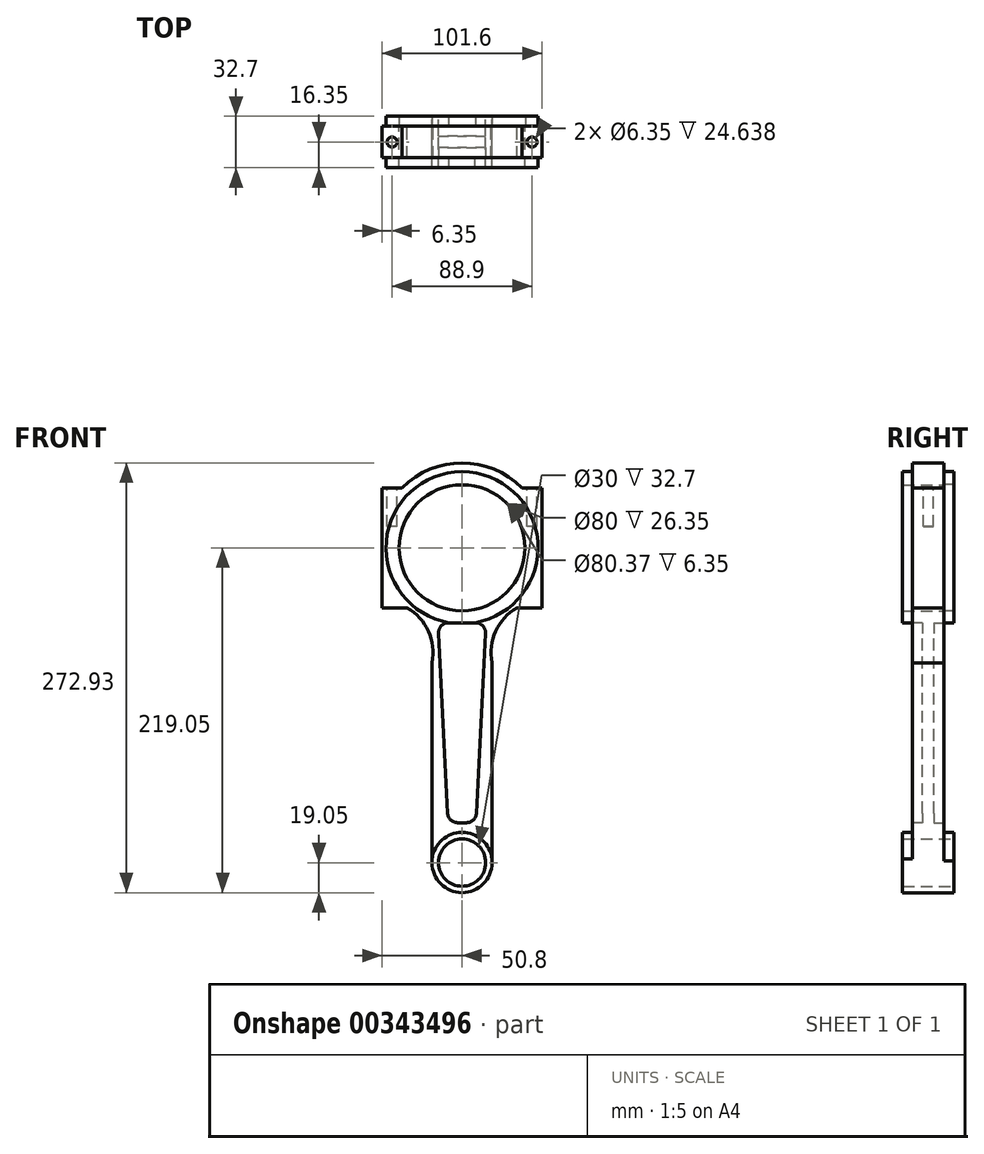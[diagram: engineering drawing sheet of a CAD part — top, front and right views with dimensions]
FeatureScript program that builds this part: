
annotation { "Feature Type Name" : "Feature", "Feature Type Description" : "" }
export const myFeature = defineFeature(function(context is Context, id is Id, definition is map)
    precondition{}
    {
        {
            var Q0;
            Q0=qCreatedBy(makeId("Front.planeOp"),FACE);
            var sketch = newSketch(context, id + "F0", { "sketchPlane" : qUnion([Q0])});
            skCircle(sketch, "E0", {"center": v(0, 0) * mm, "radius": 15 * mm});
            skCircle(sketch, "E1", {"center": v(0, 200) * mm, "radius": 40 * mm});
            skLineSegment(sketch, "E2", {"start": v(-50.8, 238.1) * mm, "end": v(-50.8, 161.9) * mm});
            skLineSegment(sketch, "E3", {"start": v(-50.8, 161.9) * mm, "end": v(-34.85, 161.9) * mm});
            skArc(sketch, "E4", {"start": v(-19.05, 127) * mm, "mid": v(-21.36, 146.98) * mm, "end": v(-34.85, 161.9) * mm});
            skLineSegment(sketch, "E5", {"start": v(-19.05, 127) * mm, "end": v(-19.05, 0) * mm});
            skLineSegment(sketch, "E6.MirrorCS", {"start": v(19.05, 127) * mm, "end": v(19.05, 0) * mm});
            skArc(sketch, "E7.MirrorCS", {"start": v(19.05, 127) * mm, "mid": v(21.36, 146.98) * mm, "end": v(34.85, 161.9) * mm});
            skLineSegment(sketch, "E8.MirrorCS", {"start": v(50.8, 238.1) * mm, "end": v(50.8, 161.9) * mm});
            skLineSegment(sketch, "E9.MirrorCS", {"start": v(50.8, 161.9) * mm, "end": v(34.85, 161.9) * mm});
            skLineSegment(sketch, "E10", {"start": v(-50.8, 238.1) * mm, "end": v(-38.1, 238.1) * mm});
            skLineSegment(sketch, "E11.MirrorCS", {"start": v(50.8, 238.1) * mm, "end": v(38.1, 238.1) * mm});
            skArc(sketch, "E12", {"start": v(38.1, 238.1) * mm, "mid": v(0, 253.88) * mm, "end": v(-38.1, 238.1) * mm});
            skArc(sketch, "E13", {"start": v(-19.05, 0) * mm, "mid": v(0, -19.05) * mm, "end": v(19.05, 0) * mm});
            skSolve(sketch);
        }
        {
            var Q0;
            Q0=makeQuery(id+"F0.imprint","IMPRINT",FACE,{"disambiguationData":[TD([[makeQuery(id+"F0.imprint","IMPRINT",EDGE,{"derivedFrom":sQuery(id+"F0.wireOp",EDGE,"E0")}),-1.0]])]});
            extrude(context, id + "F1", {"entities" : qUnion([Q0]), "endBound" : BoundingType.SYMMETRIC, "depth" : 20 * mm});
        }
        {
            var Q0;
            Q0=makeQuery(id+"F1.opExtrude","CAP_FACE",FACE,{"disambiguationData":[OSD([sQuery(id+"F0.wireOp",EDGE,"E0"),sQuery(id+"F0.wireOp",EDGE,"E1"),sQuery(id+"F0.wireOp",EDGE,"E2"),sQuery(id+"F0.wireOp",EDGE,"E3"),sQuery(id+"F0.wireOp",EDGE,"E4"),sQuery(id+"F0.wireOp",EDGE,"E5"),sQuery(id+"F0.wireOp",EDGE,"E6.MirrorCS"),sQuery(id+"F0.wireOp",EDGE,"E7.MirrorCS"),sQuery(id+"F0.wireOp",EDGE,"E8.MirrorCS"),sQuery(id+"F0.wireOp",EDGE,"E9.MirrorCS"),sQuery(id+"F0.wireOp",EDGE,"E10"),sQuery(id+"F0.wireOp",EDGE,"E11.MirrorCS"),sQuery(id+"F0.wireOp",EDGE,"E12"),sQuery(id+"F0.wireOp",EDGE,"E13")])],"isStart":true});
            var sketch = newSketch(context, id + "F2", { "sketchPlane" : qUnion([Q0])});
            skLineSegment(sketch, "E14", {"start": v(-8.56, 152.4) * mm, "end": v(8.56, 152.4) * mm});
            skLineSegment(sketch, "E15", {"start": v(14.9, 145.73) * mm, "end": v(9.2, 31.43) * mm});
            skLineSegment(sketch, "E16", {"start": v(2.85, 25.4) * mm, "end": v(-2.85, 25.4) * mm});
            skLineSegment(sketch, "E17", {"start": v(-9.2, 31.43) * mm, "end": v(-14.9, 145.73) * mm});
            skPoint(sketch, "E18.visualSharp", {"position": v(-15.24, 152.4) * mm});
            skArc(sketch, "E18.filletArc", {"start": v(-8.56, 152.4) * mm, "mid": v(-13.17, 150.43) * mm, "end": v(-14.9, 145.73) * mm});
            skPoint(sketch, "E19.visualSharp", {"position": v(15.24, 152.4) * mm});
            skArc(sketch, "E19.filletArc", {"start": v(14.9, 145.73) * mm, "mid": v(13.17, 150.43) * mm, "end": v(8.56, 152.4) * mm});
            skPoint(sketch, "E20.visualSharp", {"position": v(-8.9, 25.4) * mm});
            skArc(sketch, "E20.filletArc", {"start": v(-9.2, 31.43) * mm, "mid": v(-7.23, 27.15) * mm, "end": v(-2.85, 25.4) * mm});
            skPoint(sketch, "E21.visualSharp", {"position": v(8.89, 25.4) * mm});
            skArc(sketch, "E21.filletArc", {"start": v(2.85, 25.4) * mm, "mid": v(7.23, 27.15) * mm, "end": v(9.2, 31.43) * mm});
            skSolve(sketch);
        }
        {
            var Q0;
            Q0=makeQuery(id+"F2.imprint","IMPRINT",FACE,{"disambiguationData":[TD([[makeQuery(id+"F2.imprint","IMPRINT",EDGE,{"derivedFrom":sQuery(id+"F2.wireOp",EDGE,"E14")}),-1.0]])]});
            extrude(context, id + "F3", {"entities" : qUnion([Q0]), "operationType" : NewBodyOperationType.REMOVE, "oppositeDirection" : true, "depth" : 6.35 * mm});
        }
        {
            var Q0;
            Q0=makeQuery(id+"F1.opExtrude","CAP_FACE",FACE,{"disambiguationData":[OSD([sQuery(id+"F0.wireOp",EDGE,"E0"),sQuery(id+"F0.wireOp",EDGE,"E1"),sQuery(id+"F0.wireOp",EDGE,"E2"),sQuery(id+"F0.wireOp",EDGE,"E3"),sQuery(id+"F0.wireOp",EDGE,"E4"),sQuery(id+"F0.wireOp",EDGE,"E5"),sQuery(id+"F0.wireOp",EDGE,"E6.MirrorCS"),sQuery(id+"F0.wireOp",EDGE,"E7.MirrorCS"),sQuery(id+"F0.wireOp",EDGE,"E8.MirrorCS"),sQuery(id+"F0.wireOp",EDGE,"E9.MirrorCS"),sQuery(id+"F0.wireOp",EDGE,"E10"),sQuery(id+"F0.wireOp",EDGE,"E11.MirrorCS"),sQuery(id+"F0.wireOp",EDGE,"E12"),sQuery(id+"F0.wireOp",EDGE,"E13")])],"isStart":false});
            var sketch = newSketch(context, id + "F4", { "sketchPlane" : qUnion([Q0])});
            skLineSegment(sketch, "E22", {"start": v(-8.57, 152.4) * mm, "end": v(8.56, 152.4) * mm});
            skLineSegment(sketch, "E23", {"start": v(14.9, 145.73) * mm, "end": v(9.19, 31.43) * mm});
            skLineSegment(sketch, "E24", {"start": v(2.84, 25.4) * mm, "end": v(-2.85, 25.4) * mm});
            skLineSegment(sketch, "E25", {"start": v(-9.2, 31.43) * mm, "end": v(-14.91, 145.73) * mm});
            skPoint(sketch, "E26.visualSharp", {"position": v(-15.24, 152.4) * mm});
            skArc(sketch, "E26.filletArc", {"start": v(-8.57, 152.4) * mm, "mid": v(-13.17, 150.43) * mm, "end": v(-14.91, 145.73) * mm});
            skPoint(sketch, "E27.visualSharp", {"position": v(15.24, 152.4) * mm});
            skArc(sketch, "E27.filletArc", {"start": v(14.9, 145.73) * mm, "mid": v(13.16, 150.43) * mm, "end": v(8.56, 152.4) * mm});
            skPoint(sketch, "E28.visualSharp", {"position": v(-8.9, 25.4) * mm});
            skArc(sketch, "E28.filletArc", {"start": v(-9.2, 31.43) * mm, "mid": v(-7.23, 27.15) * mm, "end": v(-2.85, 25.4) * mm});
            skPoint(sketch, "E29.visualSharp", {"position": v(8.89, 25.4) * mm});
            skArc(sketch, "E29.filletArc", {"start": v(2.84, 25.4) * mm, "mid": v(7.22, 27.15) * mm, "end": v(9.19, 31.43) * mm});
            skSolve(sketch);
        }
        {
            var Q0;
            Q0=makeQuery(id+"F4.imprint","IMPRINT",FACE,{"disambiguationData":[TD([[makeQuery(id+"F4.imprint","IMPRINT",EDGE,{"derivedFrom":sQuery(id+"F4.wireOp",EDGE,"E22")}),-1.0]])]});
            extrude(context, id + "F5", {"entities" : qUnion([Q0]), "operationType" : NewBodyOperationType.REMOVE, "oppositeDirection" : true, "depth" : 6.35 * mm});
        }
        {
            var Q0;
            Q0=makeQuery(id+"F1.opExtrude","CAP_FACE",FACE,{"disambiguationData":[OSD([sQuery(id+"F0.wireOp",EDGE,"E0"),sQuery(id+"F0.wireOp",EDGE,"E1"),sQuery(id+"F0.wireOp",EDGE,"E2"),sQuery(id+"F0.wireOp",EDGE,"E3"),sQuery(id+"F0.wireOp",EDGE,"E4"),sQuery(id+"F0.wireOp",EDGE,"E5"),sQuery(id+"F0.wireOp",EDGE,"E6.MirrorCS"),sQuery(id+"F0.wireOp",EDGE,"E7.MirrorCS"),sQuery(id+"F0.wireOp",EDGE,"E8.MirrorCS"),sQuery(id+"F0.wireOp",EDGE,"E9.MirrorCS"),sQuery(id+"F0.wireOp",EDGE,"E10"),sQuery(id+"F0.wireOp",EDGE,"E11.MirrorCS"),sQuery(id+"F0.wireOp",EDGE,"E12"),sQuery(id+"F0.wireOp",EDGE,"E13")])],"isStart":false});
            var sketch = newSketch(context, id + "F6", { "sketchPlane" : qUnion([Q0])});
            skCircle(sketch, "E30", {"center": v(0, 0) * mm, "radius": 14.78 * mm});
            skCircle(sketch, "E31", {"center": v(0, 0) * mm, "radius": 19.18 * mm});
            skCircle(sketch, "E32", {"center": v(0, 200) * mm, "radius": 39.98 * mm});
            skCircle(sketch, "E33", {"center": v(0, 200) * mm, "radius": 48.3 * mm});
            skSolve(sketch);
        }
        {
            var Q0;
            Q0=makeQuery(id+"F6.imprint","IMPRINT",FACE,{"disambiguationData":[TD([[makeQuery(id+"F6.imprint","IMPRINT",EDGE,{"derivedFrom":makeQuery(id+"F1.opExtrude","CAP_EDGE",EDGE,{"disambiguationData":[OSD([sQuery(id+"F0.wireOp",EDGE,"E1")])],"isStart":false})}),-1.0]])]});
            var Q1;
            Q1=makeQuery(id+"F6.imprint","IMPRINT",FACE,{"disambiguationData":[TD([[makeQuery(id+"F6.imprint","IMPRINT",EDGE,{"derivedFrom":makeQuery(id+"F1.opExtrude","CAP_EDGE",EDGE,{"disambiguationData":[OSD([sQuery(id+"F0.wireOp",EDGE,"E0")])],"isStart":false})}),-1.0]])]});
            extrude(context, id + "F7", {"entities" : qUnion([Q0, Q1]), "operationType" : NewBodyOperationType.ADD, "endBound" : BoundingType.SYMMETRIC, "depth" : 12.7 * mm});
        }
        {
            var Q0;
            Q0=makeQuery(id+"F1.opExtrude","CAP_FACE",FACE,{"disambiguationData":[OSD([sQuery(id+"F0.wireOp",EDGE,"E0"),sQuery(id+"F0.wireOp",EDGE,"E1"),sQuery(id+"F0.wireOp",EDGE,"E2"),sQuery(id+"F0.wireOp",EDGE,"E3"),sQuery(id+"F0.wireOp",EDGE,"E4"),sQuery(id+"F0.wireOp",EDGE,"E5"),sQuery(id+"F0.wireOp",EDGE,"E6.MirrorCS"),sQuery(id+"F0.wireOp",EDGE,"E7.MirrorCS"),sQuery(id+"F0.wireOp",EDGE,"E8.MirrorCS"),sQuery(id+"F0.wireOp",EDGE,"E9.MirrorCS"),sQuery(id+"F0.wireOp",EDGE,"E10"),sQuery(id+"F0.wireOp",EDGE,"E11.MirrorCS"),sQuery(id+"F0.wireOp",EDGE,"E12"),sQuery(id+"F0.wireOp",EDGE,"E13")])],"isStart":true});
            var sketch = newSketch(context, id + "F8", { "sketchPlane" : qUnion([Q0])});
            skCircle(sketch, "E34", {"center": v(0, 0) * mm, "radius": 14.94 * mm});
            skCircle(sketch, "E35", {"center": v(0, 0) * mm, "radius": 19.1 * mm});
            skCircle(sketch, "E36", {"center": v(0, 200) * mm, "radius": 40.19 * mm});
            skCircle(sketch, "E37", {"center": v(0, 200) * mm, "radius": 48.36 * mm});
            skSolve(sketch);
        }
        {
            var Q0;
            Q0=makeQuery(id+"F8.imprint","IMPRINT",FACE,{"disambiguationData":[TD([[makeQuery(id+"F8.imprint","IMPRINT",EDGE,{"derivedFrom":sQuery(id+"F8.wireOp",EDGE,"E36")}),-1.0]])]});
            var Q1;
            Q1=makeQuery(id+"F8.imprint","IMPRINT",FACE,{"disambiguationData":[TD([[makeQuery(id+"F8.imprint","IMPRINT",EDGE,{"derivedFrom":makeQuery(id+"F1.opExtrude","CAP_EDGE",EDGE,{"disambiguationData":[OSD([sQuery(id+"F0.wireOp",EDGE,"E0")])],"isStart":true})}),1.0]])]});
            extrude(context, id + "F9", {"entities" : qUnion([Q0, Q1]), "operationType" : NewBodyOperationType.ADD, "endBound" : BoundingType.SYMMETRIC, "depth" : 12.7 * mm});
        }
        {
            var Q0;
            Q0=makeQuery(id+"F1.opExtrude","SWEPT_FACE",FACE,{"disambiguationData":[OSD([sQuery(id+"F0.wireOp",EDGE,"E11.MirrorCS")])]});
            var sketch = newSketch(context, id + "F10", { "sketchPlane" : qUnion([Q0])});
            skCircle(sketch, "E38", {"center": v(44.45, 0) * mm, "radius": 3.18 * mm});
            skCircle(sketch, "E39", {"center": v(-44.45, 0) * mm, "radius": 3.18 * mm});
            skSolve(sketch);
        }
        {
            var Q0;
            Q0=makeQuery(id+"F10.imprint","IMPRINT",FACE,{"disambiguationData":[TD([[makeQuery(id+"F10.imprint","IMPRINT",EDGE,{"derivedFrom":sQuery(id+"F10.wireOp",EDGE,"E39")}),1.0]])]});
            var Q1;
            Q1=makeQuery(id+"F10.imprint","IMPRINT",FACE,{"disambiguationData":[TD([[makeQuery(id+"F10.imprint","IMPRINT",EDGE,{"derivedFrom":sQuery(id+"F10.wireOp",EDGE,"E38")}),1.0]])]});
            extrude(context, id + "F11", {"entities" : qUnion([Q0, Q1]), "operationType" : NewBodyOperationType.REMOVE, "oppositeDirection" : true, "depth" : 24.64 * mm});
        }
    });
